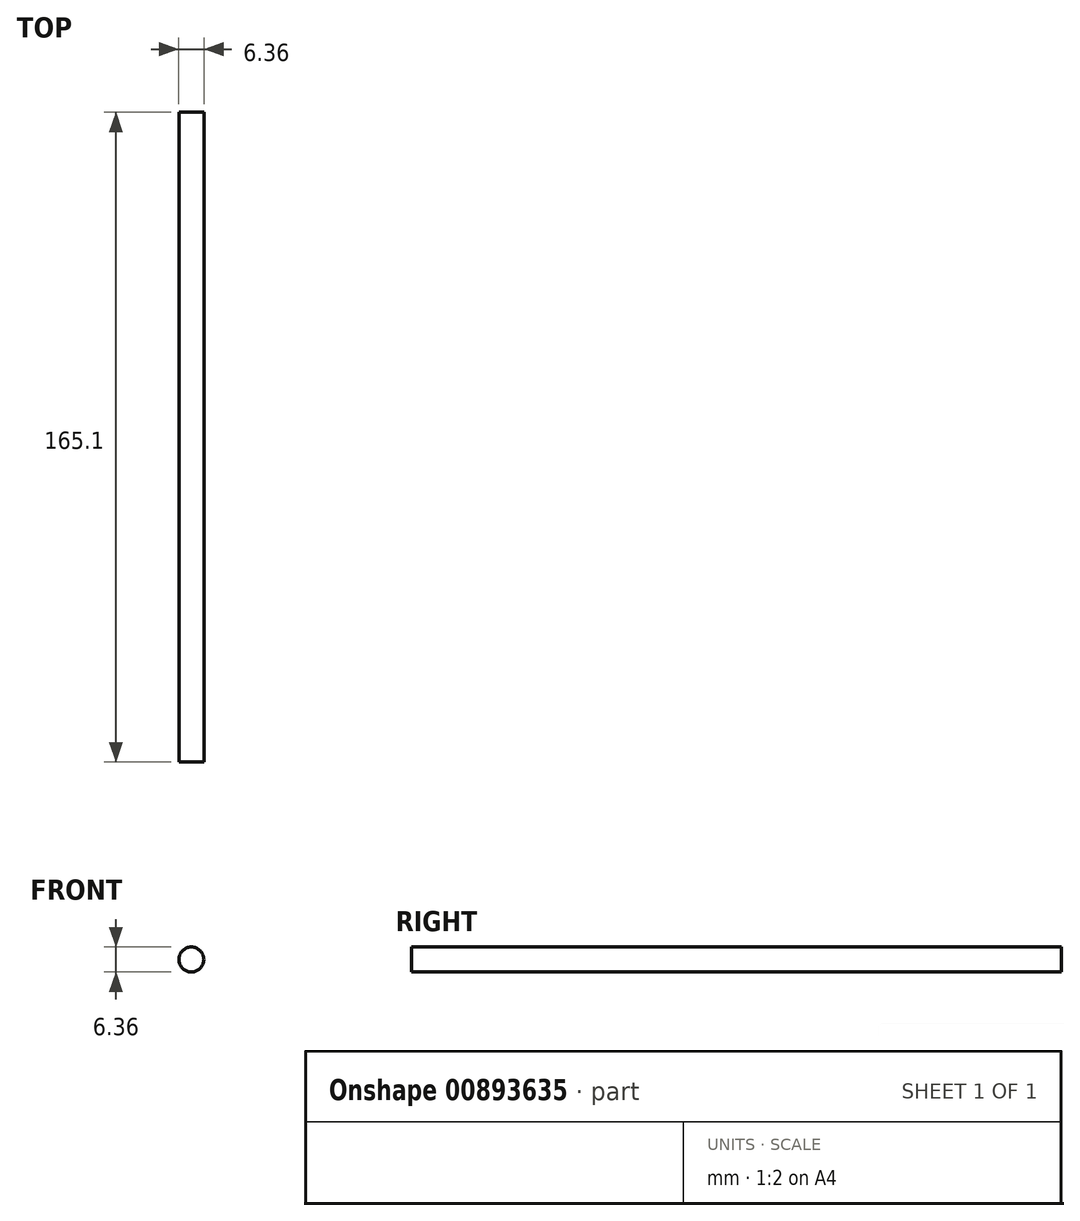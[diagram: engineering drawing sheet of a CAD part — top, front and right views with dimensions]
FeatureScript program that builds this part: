
annotation { "Feature Type Name" : "Feature", "Feature Type Description" : "" }
export const myFeature = defineFeature(function(context is Context, id is Id, definition is map)
    precondition{}
    {
        {
            var Q0;
            Q0=qCreatedBy(makeId("Front.planeOp"),FACE);
            var sketch = newSketch(context, id + "F0", { "sketchPlane" : qUnion([Q0])});
            skCircle(sketch, "E0", {"center": v(0, 0) * mm, "radius": 3.18 * mm});
            skSolve(sketch);
        }
        {
            var Q0;
            Q0=makeQuery(id+"F0.imprint","IMPRINT",FACE,{"disambiguationData":[TD([[makeQuery(id+"F0.imprint","IMPRINT",EDGE,{"derivedFrom":sQuery(id+"F0.wireOp",EDGE,"E0")}),1.0]])]});
            extrude(context, id + "F1", {"entities" : qUnion([Q0]), "endBound" : BoundingType.SYMMETRIC, "depth" : 165.1 * mm, "offsetDistance" : 25.4 * mm});
        }
    });
